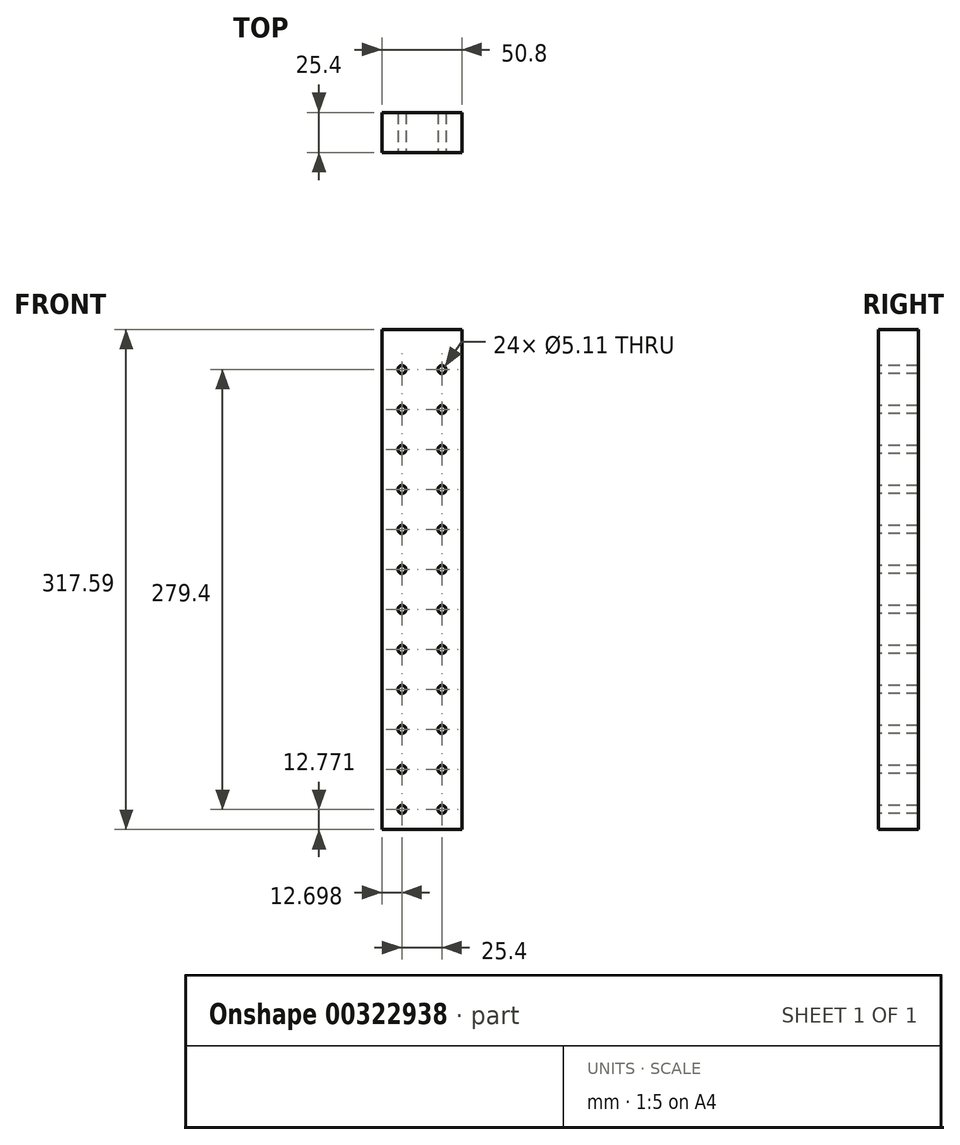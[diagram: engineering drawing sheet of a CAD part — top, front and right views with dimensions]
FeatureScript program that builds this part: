
annotation { "Feature Type Name" : "Feature", "Feature Type Description" : "" }
export const myFeature = defineFeature(function(context is Context, id is Id, definition is map)
    precondition{}
    {
        {
            var Q0;
            Q0=qCreatedBy(makeId("Front.planeOp"),FACE);
            var sketch = newSketch(context, id + "F0", { "sketchPlane" : qUnion([Q0])});
            skLineSegment(sketch, "E0", {"start": v(-34.74, -173.96) * mm, "end": v(-34.74, 143.54) * mm});
            skLineSegment(sketch, "E1", {"start": v(16.06, -174.05) * mm, "end": v(16.06, 143.45) * mm});
            skLineSegment(sketch, "E2", {"start": v(-34.74, -173.96) * mm, "end": v(16.06, -174.05) * mm});
            skLineSegment(sketch, "E3", {"start": v(-34.74, 143.54) * mm, "end": v(16.06, 143.45) * mm});
            skSolve(sketch);
        }
        {
            var Q0;
            Q0 = qSketchRegion(id + "F0", true);
            extrude(context, id + "F1", {"entities" : qUnion([Q0]), "depth" : 25.4 * mm});
        }
        {
            var Q0;
            Q0=makeQuery(id+"F1.opExtrude","CAP_FACE",FACE,{"disambiguationData":[OSD([sQuery(id+"F0.wireOp",EDGE,"E0"),sQuery(id+"F0.wireOp",EDGE,"E1"),sQuery(id+"F0.wireOp",EDGE,"E2"),sQuery(id+"F0.wireOp",EDGE,"YYH7HocC-FZVq-tuA2-h1Oj-OmbBnE2RIKpb")])],"isStart":false});
            var sketch = newSketch(context, id + "F2", { "sketchPlane" : qUnion([Q0])});
            skCircle(sketch, "E4", {"center": v(-22.04, -161.28) * mm, "radius": 2.55 * mm});
            skCircle(sketch, "E5.0.1.0", {"center": v(-22.04, -135.88) * mm, "radius": 2.55 * mm});
            skCircle(sketch, "E5.0.2.0", {"center": v(-22.04, -110.48) * mm, "radius": 2.55 * mm});
            skCircle(sketch, "E5.0.3.0", {"center": v(-22.04, -85.08) * mm, "radius": 2.55 * mm});
            skCircle(sketch, "E5.0.4.0", {"center": v(-22.04, -59.68) * mm, "radius": 2.55 * mm});
            skCircle(sketch, "E5.0.5.0", {"center": v(-22.04, -34.28) * mm, "radius": 2.55 * mm});
            skCircle(sketch, "E5.0.6.0", {"center": v(-22.04, -8.88) * mm, "radius": 2.55 * mm});
            skCircle(sketch, "E5.0.7.0", {"center": v(-22.04, 16.52) * mm, "radius": 2.55 * mm});
            skCircle(sketch, "E5.0.8.0", {"center": v(-22.04, 41.92) * mm, "radius": 2.55 * mm});
            skCircle(sketch, "E5.0.9.0", {"center": v(-22.04, 67.32) * mm, "radius": 2.55 * mm});
            skCircle(sketch, "E5.0.10.0", {"center": v(-22.04, 92.72) * mm, "radius": 2.55 * mm});
            skCircle(sketch, "E5.0.11.0", {"center": v(-22.04, 118.12) * mm, "radius": 2.55 * mm});
            skCircle(sketch, "E5.1.0.0", {"center": v(3.36, -161.28) * mm, "radius": 2.55 * mm});
            skCircle(sketch, "E5.1.1.0", {"center": v(3.36, -135.88) * mm, "radius": 2.55 * mm});
            skCircle(sketch, "E5.1.2.0", {"center": v(3.36, -110.48) * mm, "radius": 2.55 * mm});
            skCircle(sketch, "E5.1.3.0", {"center": v(3.36, -85.08) * mm, "radius": 2.55 * mm});
            skCircle(sketch, "E5.1.4.0", {"center": v(3.36, -59.68) * mm, "radius": 2.55 * mm});
            skCircle(sketch, "E5.1.5.0", {"center": v(3.36, -34.28) * mm, "radius": 2.55 * mm});
            skCircle(sketch, "E5.1.6.0", {"center": v(3.36, -8.88) * mm, "radius": 2.55 * mm});
            skCircle(sketch, "E5.1.7.0", {"center": v(3.36, 16.52) * mm, "radius": 2.55 * mm});
            skCircle(sketch, "E5.1.8.0", {"center": v(3.36, 41.92) * mm, "radius": 2.55 * mm});
            skCircle(sketch, "E5.1.9.0", {"center": v(3.36, 67.32) * mm, "radius": 2.55 * mm});
            skCircle(sketch, "E5.1.10.0", {"center": v(3.36, 92.72) * mm, "radius": 2.55 * mm});
            skCircle(sketch, "E5.1.11.0", {"center": v(3.36, 118.12) * mm, "radius": 2.55 * mm});
            skLineSegment(sketch, "E5.direction1", {"start": v(-22.04, -161.28) * mm, "end": v(3.36, -161.28) * mm, "construction": true});
            skLineSegment(sketch, "E5.direction2", {"start": v(-22.04, -161.28) * mm, "end": v(-22.04, -135.88) * mm, "construction": true});
            skCircle(sketch, "E6.0.0.13", {"center": v(-22.04, 168.92) * mm, "radius": 2.55 * mm});
            skCircle(sketch, "E6.0.0.14", {"center": v(-22.04, 194.32) * mm, "radius": 2.55 * mm});
            skCircle(sketch, "E6.0.1.13", {"center": v(3.36, 168.92) * mm, "radius": 2.55 * mm});
            skCircle(sketch, "E6.0.1.14", {"center": v(3.36, 194.32) * mm, "radius": 2.55 * mm});
            skSolve(sketch);
        }
        {
            var Q0;
            Q0 = qSketchRegion(id + "F2", true);
            extrude(context, id + "F3", {"entities" : qUnion([Q0]), "operationType" : NewBodyOperationType.REMOVE, "oppositeDirection" : true, "depth" : 508 * mm});
        }
    });
